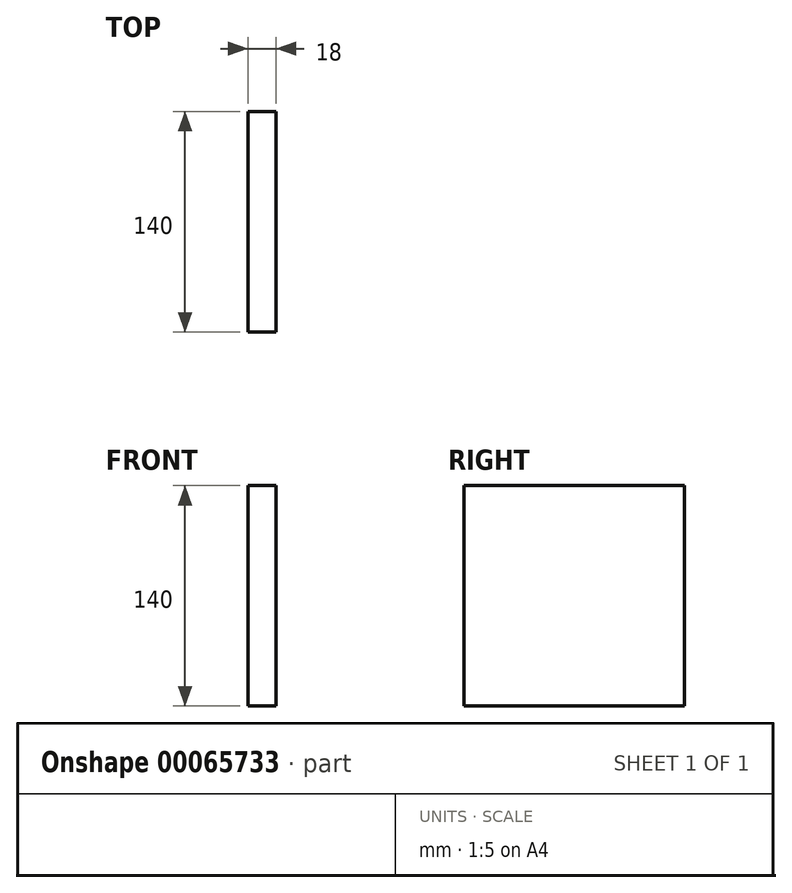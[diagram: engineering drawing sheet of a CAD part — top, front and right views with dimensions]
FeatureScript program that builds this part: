
annotation { "Feature Type Name" : "Feature", "Feature Type Description" : "" }
export const myFeature = defineFeature(function(context is Context, id is Id, definition is map)
    precondition{}
    {
        {
            var Q0;
            Q0=qCreatedBy(makeId("Right.planeOp"),FACE);
            var sketch = newSketch(context, id + "F0", { "sketchPlane" : qUnion([Q0])});
            skLineSegment(sketch, "E0.bottom", {"start": v(0, 0) * mm, "end": v(-140, 0) * mm});
            skLineSegment(sketch, "E0.top", {"start": v(0, -140) * mm, "end": v(-140, -140) * mm});
            skLineSegment(sketch, "E0.left", {"start": v(0, 0) * mm, "end": v(0, -140) * mm});
            skLineSegment(sketch, "E0.right", {"start": v(-140, 0) * mm, "end": v(-140, -140) * mm});
            skSolve(sketch);
        }
        {
            var Q0;
            Q0 = qSketchRegion(id + "F0", true);
            extrude(context, id + "F1", {"entities" : qUnion([Q0]), "depth" : 18 * mm});
        }
    });
